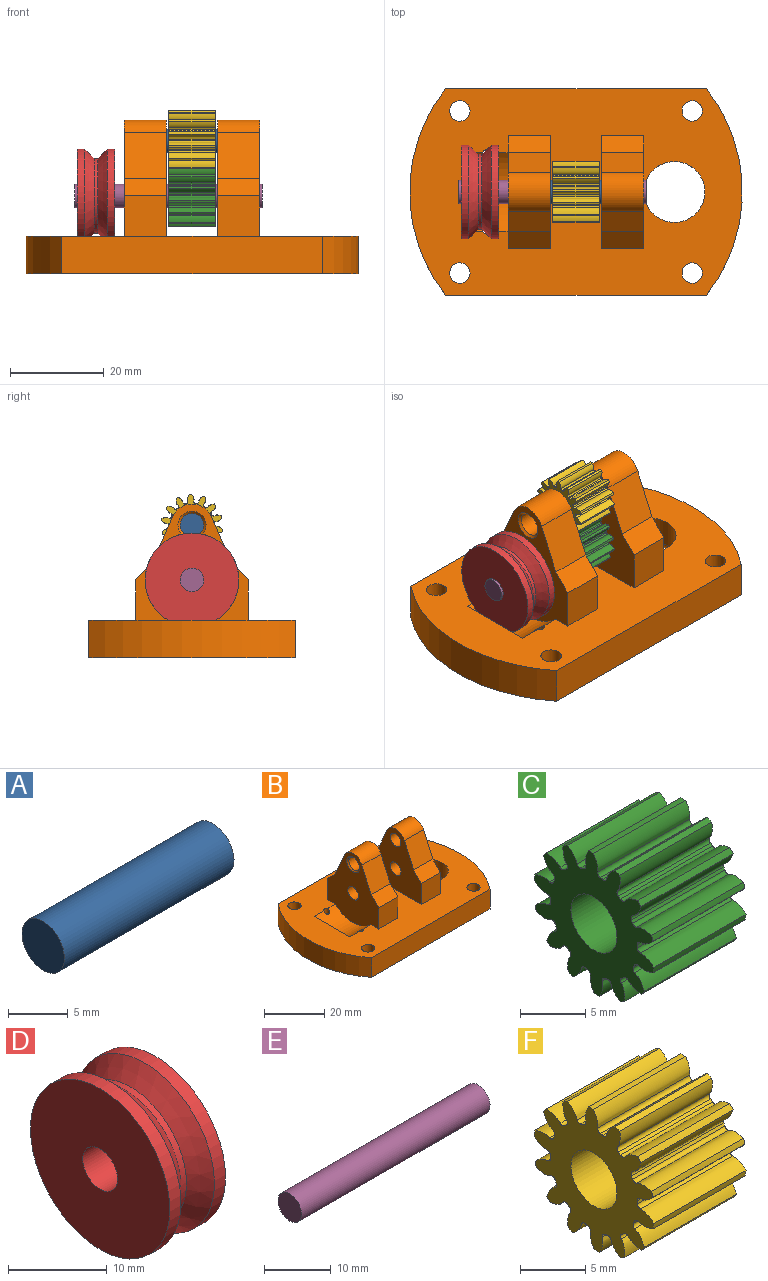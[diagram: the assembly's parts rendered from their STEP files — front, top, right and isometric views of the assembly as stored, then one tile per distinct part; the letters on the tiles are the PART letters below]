
ASSEMBLY  parts=6 mates=5
PART A: 3 faces, bbox 20x5x5 mm
  f0: cylinder r=2.5mm len=20mm, axis (-1,0,0), area 314.2mm2, adj f1,f2
  f1: plane 5x5mm, normal (1,0,0), area 19.6mm2, adj f0
  f2: plane 5x5mm, normal (-1,0,0), area 19.6mm2, adj f0
PART B: 47 faces, bbox 71x44x32.8 mm
  f0: plane 9.82x9mm, normal (0,-0.92,0.4), area 96.5mm2, adj f1,f7,f9,f10
  f1: plane 9x3.68mm, normal (0,-0.72,0.7), area 46.3mm2, adj f0,f2,f9,f10
  f2: plane 9x8.6mm, normal (0,-1,0), area 77.4mm2, adj f1,f9,f10,f11
  f3: plane 9x8.6mm, normal (0,1,0), area 77.4mm2, adj f4,f9,f10,f11
  f4: plane 9x3.68mm, normal (0,0.72,0.7), area 46.3mm2, adj f3,f5,f9,f10
  f5: plane 9.82x9mm, normal (0,0.92,0.4), area 96.5mm2, adj f4,f7,f9,f10
  f6: cylinder r=2.5mm len=8.5mm, axis (1,0,0), area 133.5mm2, adj f9,f44
  f7: cylinder r=4.5mm len=9mm, axis (1,0,0), area 93.8mm2, adj f0,f5,f9,f10
  f8: cylinder r=2.5mm len=8.5mm, axis (1,0,0), area 133.5mm2, adj f9,f43
  f9: plane 24.8x24.03mm, normal (-1,0,0), area 381.8mm2, adj f0,f1,f2,f3,f4,f5,f6,f7
  f10: plane 24.8x24.03mm, normal (1,0,0), area 364.6mm2, adj f0,f1,f2,f3,f4,f5,f7,f11
  f11: plane 71x44.03mm, normal (0,0,1), area 2117.9mm2, adj f2,f3,f9,f10,f14,f15,f21,f22
  f12: plane 9.82x9mm, normal (0,-0.92,0.4), area 96.5mm2, adj f13,f19,f21,f22
  f13: plane 9x3.68mm, normal (0,-0.72,0.7), area 46.3mm2, adj f12,f14,f21,f22
  f14: plane 9x8.6mm, normal (0,-1,0), area 77.4mm2, adj f11,f13,f21,f22
  f15: plane 9x8.6mm, normal (0,1,0), area 77.4mm2, adj f11,f16,f21,f22
  f16: plane 9x3.68mm, normal (0,0.72,0.7), area 46.3mm2, adj f15,f17,f21,f22
  f17: plane 9.82x9mm, normal (0,0.92,0.4), area 96.5mm2, adj f16,f19,f21,f22
  f18: cylinder r=2.5mm len=8.5mm, axis (1,0,0), area 133.5mm2, adj f22,f45
  f19: cylinder r=4.5mm len=9mm, axis (1,0,0), area 93.8mm2, adj f12,f17,f21,f22
  f20: cylinder r=2.5mm len=9mm, axis (1,0,0), area 141.4mm2, adj f21,f22
  f21: plane 28.2x24.03mm, normal (-1,0,0), area 412.4mm2, adj f11,f12,f13,f14,f15,f16,f17,f19
  f22: plane 24.8x24.03mm, normal (1,0,0), area 381.8mm2, adj f11,f12,f13,f14,f15,f16,f17,f18
  f23: cylinder r=35.5mm len=44.03mm, axis (0,0,1), area 379.9mm2, adj f11,f24,f30,f31
  f24: plane 55.7x8mm, normal (0,1,0), area 445.6mm2, adj f11,f23,f25,f31
  f25: cylinder r=35.5mm len=44.03mm, axis (0,0,1), area 379.9mm2, adj f11,f24,f30,f31
  f26: cylinder r=2.18mm len=8mm, axis (0,0,1), area 109.8mm2, adj f11,f31
  f27: cylinder r=2.18mm len=8mm, axis (0,0,1), area 109.8mm2, adj f11,f31
  f28: cylinder r=2.18mm len=8mm, axis (0,0,1), area 109.8mm2, adj f11,f31
  f29: cylinder r=2.18mm len=8mm, axis (0,0,1), area 109.8mm2, adj f11,f31
  f30: plane 55.7x8mm, normal (0,-1,0), area 445.6mm2, adj f11,f23,f25,f31
  f31: plane 71x44.03mm, normal (0,0,-1), area 2524.7mm2, adj f23,f24,f25,f26,f27,f28,f29,f30
  f32: plane 16.74x3.4mm, normal (1,0,0), area 39.2mm2, adj f11,f33
  f33: cylinder r=12mm len=16.74mm, axis (1,0,0), area 179.2mm2, adj f11,f21,f32,f39,f40
  f34: cylinder r=6.5mm len=13mm, axis (0,0,-1), area 245mm2, adj f11,f46
  f35: cylinder r=4mm len=8mm, axis (0,0,-1), area 125.7mm2, adj f31,f36
  f36: plane 8x8mm, normal (0,0,-1), area 37.7mm2, adj f35,f42
  f37: cylinder r=4mm len=8mm, axis (0,0,-1), area 125.7mm2, adj f31,f38
  f38: plane 8x8mm, normal (0,0,-1), area 37.7mm2, adj f37,f41
  f39: cylinder r=1mm len=2mm, axis (0,0,-1), area 9.7mm2, adj f11,f33,f41
  f40: cylinder r=1mm len=2mm, axis (0,0,-1), area 9.7mm2, adj f11,f33,f42
  f41: cone r=1mm half-angle=45deg, axis (0,0,-1), area 13.3mm2, adj f38,f39
  f42: cone r=1mm half-angle=45deg, axis (0,0,-1), area 13.3mm2, adj f36,f40
  f43: cone r=2.5mm half-angle=45deg, axis (1,0,0), area 12.2mm2, adj f8,f10
  f44: cone r=2.5mm half-angle=45deg, axis (1,0,0), area 12.2mm2, adj f6,f10
  f45: cone r=3mm half-angle=45deg, axis (-1,0,0), area 12.2mm2, adj f18,f21
  f46: torus R=8.5mm, axis (0,0,-1), area 142.7mm2, adj f31,f34
PART C: 87 faces, bbox 10x13x13.1 mm
  f0: cylinder r=6.57mm len=10mm, axis (-1,0,0), area 5.3mm2, adj f13,f16,f78,f82
  f1: cylinder r=6.57mm len=10mm, axis (-1,0,0), area 5.3mm2, adj f13,f16,f18,f77
  f2: cylinder r=6.57mm len=10mm, axis (-1,0,0), area 5.3mm2, adj f13,f16,f72,f83
  f3: cylinder r=6.57mm len=10mm, axis (-1,0,0), area 5.3mm2, adj f13,f16,f67,f73
  f4: cylinder r=6.57mm len=10mm, axis (-1,0,0), area 5.3mm2, adj f13,f16,f58,f62
  f5: cylinder r=6.57mm len=10mm, axis (-1,0,0), area 5.3mm2, adj f13,f16,f57,f68
  f6: cylinder r=6.57mm len=10mm, axis (-1,0,0), area 5.3mm2, adj f13,f16,f52,f63
  f7: cylinder r=6.57mm len=10mm, axis (-1,0,0), area 5.3mm2, adj f13,f16,f47,f53
  f8: cylinder r=6.57mm len=10mm, axis (-1,0,0), area 5.3mm2, adj f13,f16,f38,f42
  f9: cylinder r=6.57mm len=10mm, axis (-1,0,0), area 5.3mm2, adj f13,f16,f33,f37
  f10: cylinder r=6.57mm len=10mm, axis (-1,0,0), area 5.3mm2, adj f13,f16,f28,f32
  f11: cylinder r=6.57mm len=10mm, axis (-1,0,0), area 5.3mm2, adj f13,f16,f23,f27
  f12: cylinder r=6.57mm len=10mm, axis (-1,0,0), area 5.3mm2, adj f13,f16,f22,f48
  f13: plane 13.14x13.02mm, normal (1,0,0), area 81mm2, adj f0,f1,f2,f3,f4,f5,f6,f7
  f14: cylinder r=2.5mm len=10mm, axis (-1,0,0), area 157.1mm2, adj f13,f16
  f15: cylinder r=6.57mm len=10mm, axis (-1,0,0), area 5.3mm2, adj f13,f16,f17,f43
  f16: plane 13.14x13.02mm, normal (-1,0,0), area 81mm2, adj f0,f1,f2,f3,f4,f5,f6,f7
  f17: extruded ~10x1.4mm, area 16.6mm2, adj f13,f15,f16,f21
  f18: extruded ~10x1.47mm, area 16.6mm2, adj f1,f13,f16,f20
  f19: cylinder r=4.72mm len=10mm, axis (-1,0,0), area 2.9mm2, adj f13,f16,f20,f21
  f20: cylinder r=0.34mm len=10mm, axis (-1,0,0), area 5.1mm2, adj f13,f16,f18,f19
  f21: cylinder r=0.34mm len=10mm, axis (-1,0,0), area 5.1mm2, adj f13,f16,f17,f19
  f22: extruded ~10x1.48mm, area 16.6mm2, adj f12,f13,f16,f26
  f23: extruded ~10x1.55mm, area 16.6mm2, adj f11,f13,f16,f25
  f24: cylinder r=4.72mm len=10mm, axis (-1,0,0), area 2.9mm2, adj f13,f16,f25,f26
  f25: cylinder r=0.34mm len=10mm, axis (-1,0,0), area 5.1mm2, adj f13,f16,f23,f24
  f26: cylinder r=0.34mm len=10mm, axis (-1,0,0), area 5.1mm2, adj f13,f16,f22,f24
  f27: extruded ~10x1.19mm, area 16.6mm2, adj f11,f13,f16,f31
  f28: extruded ~10x1.57mm, area 16.6mm2, adj f10,f13,f16,f30
  f29: cylinder r=4.72mm len=10mm, axis (-1,0,0), area 2.9mm2, adj f13,f16,f30,f31
  f30: cylinder r=0.34mm len=10mm, axis (-1,0,0), area 5.1mm2, adj f13,f16,f28,f29
  f31: cylinder r=0.34mm len=10mm, axis (-1,0,0), area 5.1mm2, adj f13,f16,f27,f29
  f32: extruded ~10x1.54mm, area 16.6mm2, adj f10,f13,f16,f36
  f33: extruded ~10x1.29mm, area 16.6mm2, adj f9,f13,f16,f35
  f34: cylinder r=4.72mm len=10mm, axis (-1,0,0), area 2.9mm2, adj f13,f16,f35,f36
  f35: cylinder r=0.34mm len=10mm, axis (-1,0,0), area 5.1mm2, adj f13,f16,f33,f34
  f36: cylinder r=0.34mm len=10mm, axis (-1,0,0), area 5.1mm2, adj f13,f16,f32,f34
  f37: extruded ~10x1.58mm, area 16.6mm2, adj f9,f13,f16,f41
  f38: extruded ~10x1.42mm, area 16.6mm2, adj f8,f13,f16,f40
  f39: cylinder r=4.72mm len=10mm, axis (-1,0,0), area 2.9mm2, adj f13,f16,f40,f41
  f40: cylinder r=0.34mm len=10mm, axis (-1,0,0), area 5.1mm2, adj f13,f16,f38,f39
  f41: cylinder r=0.34mm len=10mm, axis (-1,0,0), area 5.1mm2, adj f13,f16,f37,f39
  f42: extruded ~10x1.31mm, area 16.6mm2, adj f8,f13,f16,f46
  f43: extruded ~10x1.6mm, area 16.6mm2, adj f13,f15,f16,f45
  f44: cylinder r=4.72mm len=10mm, axis (-1,0,0), area 2.9mm2, adj f13,f16,f45,f46
  f45: cylinder r=0.34mm len=10mm, axis (-1,0,0), area 5.1mm2, adj f13,f16,f43,f44
  f46: cylinder r=0.34mm len=10mm, axis (-1,0,0), area 5.1mm2, adj f13,f16,f42,f44
  f47: extruded ~10x1.6mm, area 16.6mm2, adj f7,f13,f16,f51
  f48: extruded ~10x1.22mm, area 16.6mm2, adj f12,f13,f16,f50
  f49: cylinder r=4.72mm len=10mm, axis (-1,0,0), area 2.9mm2, adj f13,f16,f50,f51
  f50: cylinder r=0.34mm len=10mm, axis (-1,0,0), area 5.1mm2, adj f13,f16,f48,f49
  f51: cylinder r=0.34mm len=10mm, axis (-1,0,0), area 5.1mm2, adj f13,f16,f47,f49
  f52: extruded ~10x1.4mm, area 16.6mm2, adj f6,f13,f16,f56
  f53: extruded ~10x1.47mm, area 16.6mm2, adj f7,f13,f16,f55
  f54: cylinder r=4.72mm len=10mm, axis (-1,0,0), area 2.9mm2, adj f13,f16,f55,f56
  f55: cylinder r=0.34mm len=10mm, axis (-1,0,0), area 5.1mm2, adj f13,f16,f53,f54
  f56: cylinder r=0.34mm len=10mm, axis (-1,0,0), area 5.1mm2, adj f13,f16,f52,f54
  f57: extruded ~10x1.58mm, area 16.6mm2, adj f5,f13,f16,f61
  f58: extruded ~10x1.42mm, area 16.6mm2, adj f4,f13,f16,f60
  f59: cylinder r=4.72mm len=10mm, axis (-1,0,0), area 2.9mm2, adj f13,f16,f60,f61
  f60: cylinder r=0.34mm len=10mm, axis (-1,0,0), area 5.1mm2, adj f13,f16,f58,f59
  f61: cylinder r=0.34mm len=10mm, axis (-1,0,0), area 5.1mm2, adj f13,f16,f57,f59
  f62: extruded ~10x1.31mm, area 16.6mm2, adj f4,f13,f16,f66
  f63: extruded ~10x1.6mm, area 16.6mm2, adj f6,f13,f16,f65
  f64: cylinder r=4.72mm len=10mm, axis (-1,0,0), area 2.9mm2, adj f13,f16,f65,f66
  f65: cylinder r=0.34mm len=10mm, axis (-1,0,0), area 5.1mm2, adj f13,f16,f63,f64
  f66: cylinder r=0.34mm len=10mm, axis (-1,0,0), area 5.1mm2, adj f13,f16,f62,f64
  f67: extruded ~10x1.54mm, area 16.6mm2, adj f3,f13,f16,f71
  f68: extruded ~10x1.29mm, area 16.6mm2, adj f5,f13,f16,f70
  f69: cylinder r=4.72mm len=10mm, axis (-1,0,0), area 2.9mm2, adj f13,f16,f70,f71
  f70: cylinder r=0.34mm len=10mm, axis (-1,0,0), area 5.1mm2, adj f13,f16,f68,f69
  f71: cylinder r=0.34mm len=10mm, axis (-1,0,0), area 5.1mm2, adj f13,f16,f67,f69
  f72: extruded ~10x1.19mm, area 16.6mm2, adj f2,f13,f16,f76
  f73: extruded ~10x1.57mm, area 16.6mm2, adj f3,f13,f16,f75
  f74: cylinder r=4.72mm len=10mm, axis (-1,0,0), area 2.9mm2, adj f13,f16,f75,f76
  f75: cylinder r=0.34mm len=10mm, axis (-1,0,0), area 5.1mm2, adj f13,f16,f73,f74
  f76: cylinder r=0.34mm len=10mm, axis (-1,0,0), area 5.1mm2, adj f13,f16,f72,f74
  f77: extruded ~10x1.6mm, area 16.6mm2, adj f1,f13,f16,f81
  f78: extruded ~10x1.22mm, area 16.6mm2, adj f0,f13,f16,f80
  f79: cylinder r=4.72mm len=10mm, axis (-1,0,0), area 2.9mm2, adj f13,f16,f80,f81
  f80: cylinder r=0.34mm len=10mm, axis (-1,0,0), area 5.1mm2, adj f13,f16,f78,f79
  f81: cylinder r=0.34mm len=10mm, axis (-1,0,0), area 5.1mm2, adj f13,f16,f77,f79
  f82: extruded ~10x1.48mm, area 16.6mm2, adj f0,f13,f16,f86
  f83: extruded ~10x1.55mm, area 16.6mm2, adj f2,f13,f16,f85
  f84: cylinder r=4.72mm len=10mm, axis (-1,0,0), area 2.9mm2, adj f13,f16,f85,f86
  f85: cylinder r=0.34mm len=10mm, axis (-1,0,0), area 5.1mm2, adj f13,f16,f83,f84
  f86: cylinder r=0.34mm len=10mm, axis (-1,0,0), area 5.1mm2, adj f13,f16,f82,f84
PART D: 8 faces, bbox 8x20x20 mm
  f0: cylinder r=8mm len=16mm, axis (1,0,0), area 40.2mm2, adj f6,f7
  f1: cylinder r=2.5mm len=8mm, axis (1,0,0), area 125.7mm2, adj f2,f3
  f2: plane 20x20mm, normal (-1,0,0), area 294.5mm2, adj f1,f5
  f3: plane 20x20mm, normal (1,0,0), area 294.5mm2, adj f1,f4
  f4: cylinder r=10mm len=20mm, axis (1,0,0), area 100.5mm2, adj f3,f6
  f5: cylinder r=10mm len=20mm, axis (-1,0,0), area 100.5mm2, adj f2,f7
  f6: cone r=10mm half-angle=45deg, axis (1,0,0), area 159.9mm2, adj f0,f4
  f7: cone r=8mm half-angle=45deg, axis (-1,0,0), area 159.9mm2, adj f0,f5
PART E: 3 faces, bbox 40x5x5 mm
  f0: cylinder r=2.5mm len=40mm, axis (-1,0,0), area 628.3mm2, adj f1,f2
  f1: plane 5x5mm, normal (1,0,0), area 19.6mm2, adj f0
  f2: plane 5x5mm, normal (-1,0,0), area 19.6mm2, adj f0
PART F: 87 faces, bbox 10x13x13.1 mm
  f0: cylinder r=6.57mm len=10mm, axis (-1,0,0), area 5.3mm2, adj f13,f16,f78,f82
  f1: cylinder r=6.57mm len=10mm, axis (-1,0,0), area 5.3mm2, adj f13,f16,f18,f77
  f2: cylinder r=6.57mm len=10mm, axis (-1,0,0), area 5.3mm2, adj f13,f16,f72,f83
  f3: cylinder r=6.57mm len=10mm, axis (-1,0,0), area 5.3mm2, adj f13,f16,f67,f73
  f4: cylinder r=6.57mm len=10mm, axis (-1,0,0), area 5.3mm2, adj f13,f16,f58,f62
  f5: cylinder r=6.57mm len=10mm, axis (-1,0,0), area 5.3mm2, adj f13,f16,f57,f68
  f6: cylinder r=6.57mm len=10mm, axis (-1,0,0), area 5.3mm2, adj f13,f16,f52,f63
  f7: cylinder r=6.57mm len=10mm, axis (-1,0,0), area 5.3mm2, adj f13,f16,f47,f53
  f8: cylinder r=6.57mm len=10mm, axis (-1,0,0), area 5.3mm2, adj f13,f16,f38,f42
  f9: cylinder r=6.57mm len=10mm, axis (-1,0,0), area 5.3mm2, adj f13,f16,f33,f37
  f10: cylinder r=6.57mm len=10mm, axis (-1,0,0), area 5.3mm2, adj f13,f16,f28,f32
  f11: cylinder r=6.57mm len=10mm, axis (-1,0,0), area 5.3mm2, adj f13,f16,f23,f27
  f12: cylinder r=6.57mm len=10mm, axis (-1,0,0), area 5.3mm2, adj f13,f16,f22,f48
  f13: plane 13.14x13.02mm, normal (1,0,0), area 81mm2, adj f0,f1,f2,f3,f4,f5,f6,f7
  f14: cylinder r=2.5mm len=10mm, axis (-1,0,0), area 157.1mm2, adj f13,f16
  f15: cylinder r=6.57mm len=10mm, axis (-1,0,0), area 5.3mm2, adj f13,f16,f17,f43
  f16: plane 13.14x13.02mm, normal (-1,0,0), area 81mm2, adj f0,f1,f2,f3,f4,f5,f6,f7
  f17: extruded ~10x1.4mm, area 16.6mm2, adj f13,f15,f16,f21
  f18: extruded ~10x1.47mm, area 16.6mm2, adj f1,f13,f16,f20
  f19: cylinder r=4.72mm len=10mm, axis (-1,0,0), area 2.9mm2, adj f13,f16,f20,f21
  f20: cylinder r=0.34mm len=10mm, axis (-1,0,0), area 5.1mm2, adj f13,f16,f18,f19
  f21: cylinder r=0.34mm len=10mm, axis (-1,0,0), area 5.1mm2, adj f13,f16,f17,f19
  f22: extruded ~10x1.48mm, area 16.6mm2, adj f12,f13,f16,f26
  f23: extruded ~10x1.55mm, area 16.6mm2, adj f11,f13,f16,f25
  f24: cylinder r=4.72mm len=10mm, axis (-1,0,0), area 2.9mm2, adj f13,f16,f25,f26
  f25: cylinder r=0.34mm len=10mm, axis (-1,0,0), area 5.1mm2, adj f13,f16,f23,f24
  f26: cylinder r=0.34mm len=10mm, axis (-1,0,0), area 5.1mm2, adj f13,f16,f22,f24
  f27: extruded ~10x1.19mm, area 16.6mm2, adj f11,f13,f16,f31
  f28: extruded ~10x1.57mm, area 16.6mm2, adj f10,f13,f16,f30
  f29: cylinder r=4.72mm len=10mm, axis (-1,0,0), area 2.9mm2, adj f13,f16,f30,f31
  f30: cylinder r=0.34mm len=10mm, axis (-1,0,0), area 5.1mm2, adj f13,f16,f28,f29
  f31: cylinder r=0.34mm len=10mm, axis (-1,0,0), area 5.1mm2, adj f13,f16,f27,f29
  f32: extruded ~10x1.54mm, area 16.6mm2, adj f10,f13,f16,f36
  f33: extruded ~10x1.29mm, area 16.6mm2, adj f9,f13,f16,f35
  f34: cylinder r=4.72mm len=10mm, axis (-1,0,0), area 2.9mm2, adj f13,f16,f35,f36
  f35: cylinder r=0.34mm len=10mm, axis (-1,0,0), area 5.1mm2, adj f13,f16,f33,f34
  f36: cylinder r=0.34mm len=10mm, axis (-1,0,0), area 5.1mm2, adj f13,f16,f32,f34
  f37: extruded ~10x1.58mm, area 16.6mm2, adj f9,f13,f16,f41
  f38: extruded ~10x1.42mm, area 16.6mm2, adj f8,f13,f16,f40
  f39: cylinder r=4.72mm len=10mm, axis (-1,0,0), area 2.9mm2, adj f13,f16,f40,f41
  f40: cylinder r=0.34mm len=10mm, axis (-1,0,0), area 5.1mm2, adj f13,f16,f38,f39
  f41: cylinder r=0.34mm len=10mm, axis (-1,0,0), area 5.1mm2, adj f13,f16,f37,f39
  f42: extruded ~10x1.31mm, area 16.6mm2, adj f8,f13,f16,f46
  f43: extruded ~10x1.6mm, area 16.6mm2, adj f13,f15,f16,f45
  f44: cylinder r=4.72mm len=10mm, axis (-1,0,0), area 2.9mm2, adj f13,f16,f45,f46
  f45: cylinder r=0.34mm len=10mm, axis (-1,0,0), area 5.1mm2, adj f13,f16,f43,f44
  f46: cylinder r=0.34mm len=10mm, axis (-1,0,0), area 5.1mm2, adj f13,f16,f42,f44
  f47: extruded ~10x1.6mm, area 16.6mm2, adj f7,f13,f16,f51
  f48: extruded ~10x1.22mm, area 16.6mm2, adj f12,f13,f16,f50
  f49: cylinder r=4.72mm len=10mm, axis (-1,0,0), area 2.9mm2, adj f13,f16,f50,f51
  f50: cylinder r=0.34mm len=10mm, axis (-1,0,0), area 5.1mm2, adj f13,f16,f48,f49
  f51: cylinder r=0.34mm len=10mm, axis (-1,0,0), area 5.1mm2, adj f13,f16,f47,f49
  f52: extruded ~10x1.4mm, area 16.6mm2, adj f6,f13,f16,f56
  f53: extruded ~10x1.47mm, area 16.6mm2, adj f7,f13,f16,f55
  f54: cylinder r=4.72mm len=10mm, axis (-1,0,0), area 2.9mm2, adj f13,f16,f55,f56
  f55: cylinder r=0.34mm len=10mm, axis (-1,0,0), area 5.1mm2, adj f13,f16,f53,f54
  f56: cylinder r=0.34mm len=10mm, axis (-1,0,0), area 5.1mm2, adj f13,f16,f52,f54
  f57: extruded ~10x1.58mm, area 16.6mm2, adj f5,f13,f16,f61
  f58: extruded ~10x1.42mm, area 16.6mm2, adj f4,f13,f16,f60
  f59: cylinder r=4.72mm len=10mm, axis (-1,0,0), area 2.9mm2, adj f13,f16,f60,f61
  f60: cylinder r=0.34mm len=10mm, axis (-1,0,0), area 5.1mm2, adj f13,f16,f58,f59
  f61: cylinder r=0.34mm len=10mm, axis (-1,0,0), area 5.1mm2, adj f13,f16,f57,f59
  f62: extruded ~10x1.31mm, area 16.6mm2, adj f4,f13,f16,f66
  f63: extruded ~10x1.6mm, area 16.6mm2, adj f6,f13,f16,f65
  f64: cylinder r=4.72mm len=10mm, axis (-1,0,0), area 2.9mm2, adj f13,f16,f65,f66
  f65: cylinder r=0.34mm len=10mm, axis (-1,0,0), area 5.1mm2, adj f13,f16,f63,f64
  f66: cylinder r=0.34mm len=10mm, axis (-1,0,0), area 5.1mm2, adj f13,f16,f62,f64
  f67: extruded ~10x1.54mm, area 16.6mm2, adj f3,f13,f16,f71
  f68: extruded ~10x1.29mm, area 16.6mm2, adj f5,f13,f16,f70
  f69: cylinder r=4.72mm len=10mm, axis (-1,0,0), area 2.9mm2, adj f13,f16,f70,f71
  f70: cylinder r=0.34mm len=10mm, axis (-1,0,0), area 5.1mm2, adj f13,f16,f68,f69
  f71: cylinder r=0.34mm len=10mm, axis (-1,0,0), area 5.1mm2, adj f13,f16,f67,f69
  f72: extruded ~10x1.19mm, area 16.6mm2, adj f2,f13,f16,f76
  f73: extruded ~10x1.57mm, area 16.6mm2, adj f3,f13,f16,f75
  f74: cylinder r=4.72mm len=10mm, axis (-1,0,0), area 2.9mm2, adj f13,f16,f75,f76
  f75: cylinder r=0.34mm len=10mm, axis (-1,0,0), area 5.1mm2, adj f13,f16,f73,f74
  f76: cylinder r=0.34mm len=10mm, axis (-1,0,0), area 5.1mm2, adj f13,f16,f72,f74
  f77: extruded ~10x1.6mm, area 16.6mm2, adj f1,f13,f16,f81
  f78: extruded ~10x1.22mm, area 16.6mm2, adj f0,f13,f16,f80
  f79: cylinder r=4.72mm len=10mm, axis (-1,0,0), area 2.9mm2, adj f13,f16,f80,f81
  f80: cylinder r=0.34mm len=10mm, axis (-1,0,0), area 5.1mm2, adj f13,f16,f78,f79
  f81: cylinder r=0.34mm len=10mm, axis (-1,0,0), area 5.1mm2, adj f13,f16,f77,f79
  f82: extruded ~10x1.48mm, area 16.6mm2, adj f0,f13,f16,f86
  f83: extruded ~10x1.55mm, area 16.6mm2, adj f2,f13,f16,f85
  f84: cylinder r=4.72mm len=10mm, axis (-1,0,0), area 2.9mm2, adj f13,f16,f85,f86
  f85: cylinder r=0.34mm len=10mm, axis (-1,0,0), area 5.1mm2, adj f13,f16,f83,f84
  f86: cylinder r=0.34mm len=10mm, axis (-1,0,0), area 5.1mm2, adj f13,f16,f82,f84
PLACE A t=(0.25,0,0)mm
PLACE B at identity fixed
PLACE C at identity
PLACE D t=(-1.5,0,0)mm
PLACE E at identity
PLACE F at identity
MATE fastened D.f0 <-> E.f0  axis (-1,0,0) through (-38.42,11.01,-12.4)mm
MATE fastened C.f0 <-> E.f0  axis (1,0,0) through (-8.92,11.01,-12.4)mm
MATE fastened A.f0 <-> B.f6  axis (-1,0,0) through (-23.67,11.01,-0.7)mm
MATE revolute A.f0 <-> F.f0  axis (1,0,0) through (-3.67,11.01,-0.7)mm
MATE revolute E.f0 <-> B.f8  axis (1,0,0) through (1.08,11.01,-12.4)mm
